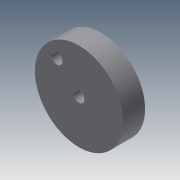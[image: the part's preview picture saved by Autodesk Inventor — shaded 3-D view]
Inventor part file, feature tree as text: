
AUTODESK INVENTOR PART (.ipt)
format: ipt  version: 2015 (Build 190159000, 159)  size: 87,552 bytes
history: native  units: mm
features: extrude x3, sketch x3
ambient origin geometry x8: Origin, YZ Plane, XZ Plane, XY Plane, X Axis, Y Axis, Z Axis, Center Point
bodies: Solid1 (feature_tree)
feature tree (6):
  extrude  "Extrusion1"  Depth=20.0mm TaperAngle=0.0deg
  extrude  "Extrusion2"  Depth=20.0mm
  extrude  "Extrusion3"  Depth=10.0mm
  sketch  "Sketch1"  dims[d0=80.0mm d1=20.0mm d2=0.0mm]
  sketch  "Sketch2"  dims[d3=10.0mm d4=20.0mm]
  sketch  "Sketch3"  dims[d5=20.0mm d6=10.0mm d7=0.0mm d8=10.0mm d9=10.0mm d10=0.0mm]
